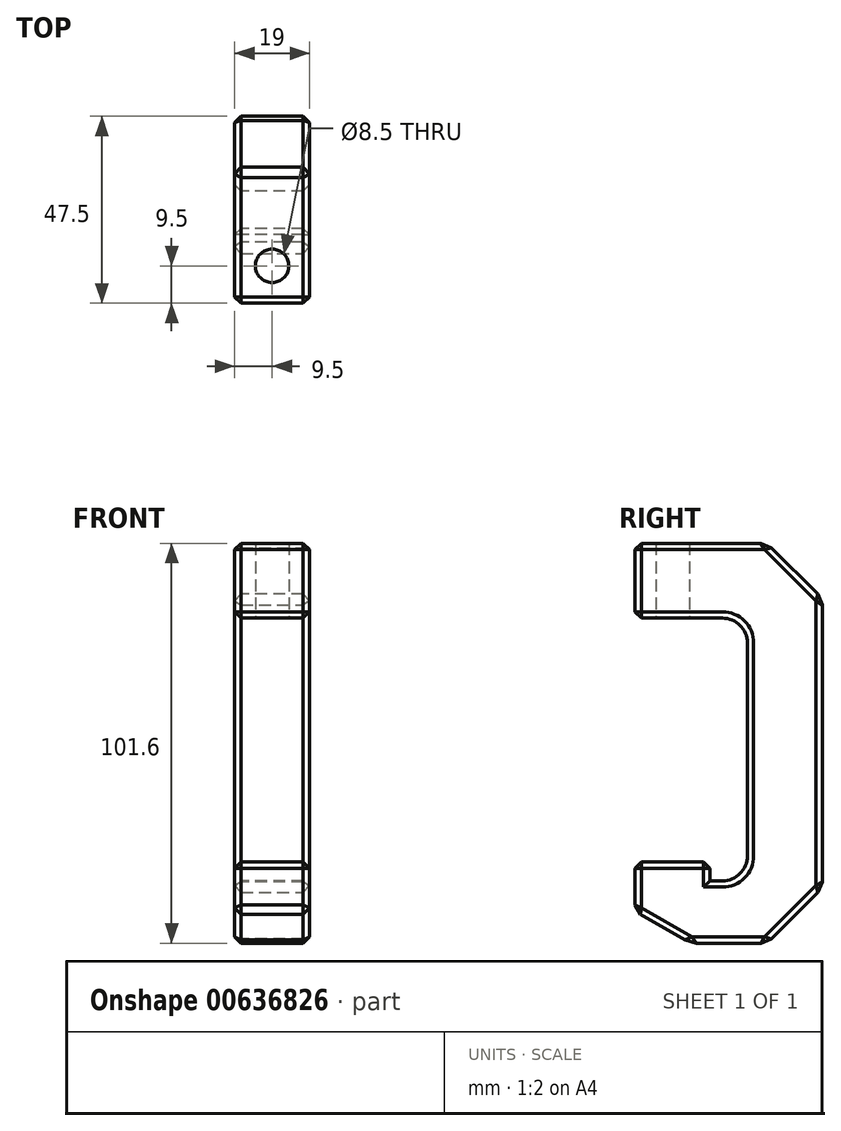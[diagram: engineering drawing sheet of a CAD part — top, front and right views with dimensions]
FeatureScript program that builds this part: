
annotation { "Feature Type Name" : "Feature", "Feature Type Description" : "" }
export const myFeature = defineFeature(function(context is Context, id is Id, definition is map)
    precondition{}
    {
        {
            var Q0;
            Q0=qCreatedBy(makeId("Right.planeOp"),FACE);
            var sketch = newSketch(context, id + "F0", { "sketchPlane" : qUnion([Q0])});
            skLineSegment(sketch, "E0", {"start": v(-33.5, 101.6) * mm, "end": v(-33.5, 82.6) * mm});
            skLineSegment(sketch, "E1", {"start": v(-33.5, 82.6) * mm, "end": v(-11.35, 82.6) * mm});
            skLineSegment(sketch, "E2", {"start": v(-5, 76.25) * mm, "end": v(-5, 22.2) * mm});
            skLineSegment(sketch, "E3", {"start": v(-11.35, 15.85) * mm, "end": v(-14.5, 15.85) * mm});
            skLineSegment(sketch, "E4", {"start": v(-33.5, 8.08) * mm, "end": v(-19.5, 0) * mm});
            skLineSegment(sketch, "E5", {"start": v(-19.5, 0) * mm, "end": v(0, 0) * mm});
            skLineSegment(sketch, "E6", {"start": v(0, 0) * mm, "end": v(14, 14) * mm});
            skLineSegment(sketch, "E7", {"start": v(14, 14) * mm, "end": v(14, 87.6) * mm});
            skLineSegment(sketch, "E8", {"start": v(14, 87.6) * mm, "end": v(0, 101.6) * mm});
            skLineSegment(sketch, "E9", {"start": v(0, 101.6) * mm, "end": v(-33.5, 101.6) * mm});
            skPoint(sketch, "E10.visualSharp", {"position": v(-5, 15.85) * mm});
            skArc(sketch, "E10.filletArc", {"start": v(-11.35, 15.85) * mm, "mid": v(-6.86, 17.7) * mm, "end": v(-5, 22.2) * mm});
            skPoint(sketch, "E11.visualSharp", {"position": v(-5, 82.6) * mm});
            skArc(sketch, "E11.filletArc", {"start": v(-5, 76.25) * mm, "mid": v(-6.86, 80.74) * mm, "end": v(-11.35, 82.6) * mm});
            skLineSegment(sketch, "E12", {"start": v(-14.5, 15.85) * mm, "end": v(-14.5, 20.65) * mm});
            skLineSegment(sketch, "E13", {"start": v(-14.5, 20.65) * mm, "end": v(-33.5, 20.65) * mm});
            skLineSegment(sketch, "E14", {"start": v(-33.5, 20.65) * mm, "end": v(-33.5, 8.08) * mm});
            skSolve(sketch);
        }
        {
            var Q0;
            Q0=makeQuery(id+"F0.imprint","IMPRINT",FACE,{"disambiguationData":[TD([[makeQuery(id+"F0.imprint","IMPRINT",EDGE,{"derivedFrom":sQuery(id+"F0.wireOp",EDGE,"E0")}),1.0]])]});
            extrude(context, id + "F1", {"entities" : qUnion([Q0]), "depth" : 19 * mm, "offsetDistance" : 25 * mm, "symmetric" : true});
        }
        {
            var Q0;
            Q0=makeQuery(id+"F1.opExtrude","SWEPT_FACE",FACE,{"disambiguationData":[OSD([sQuery(id+"F0.wireOp",EDGE,"E9")])]});
            var Q1;
            Q1=makeQuery(id+"F1.opExtrude","SWEPT_FACE",FACE,{"disambiguationData":[OSD([sQuery(id+"F0.wireOp",EDGE,"E0")])]});
            var Q2;
            Q2=makeQuery(id+"F1.opExtrude","CAP_FACE",FACE,{"disambiguationData":[OSD([sQuery(id+"F0.wireOp",EDGE,"E0"),sQuery(id+"F0.wireOp",EDGE,"E1"),sQuery(id+"F0.wireOp",EDGE,"E2"),sQuery(id+"F0.wireOp",EDGE,"E3"),sQuery(id+"F0.wireOp",EDGE,"E4"),sQuery(id+"F0.wireOp",EDGE,"E5"),sQuery(id+"F0.wireOp",EDGE,"E6"),sQuery(id+"F0.wireOp",EDGE,"E7"),sQuery(id+"F0.wireOp",EDGE,"E8"),sQuery(id+"F0.wireOp",EDGE,"E9"),sQuery(id+"F0.wireOp",EDGE,"E10.filletArc"),sQuery(id+"F0.wireOp",EDGE,"E11.filletArc"),sQuery(id+"F0.wireOp",EDGE,"E12"),sQuery(id+"F0.wireOp",EDGE,"E13"),sQuery(id+"F0.wireOp",EDGE,"E14")])],"isStart":false});
            var Q3;
            Q3=makeQuery(id+"F1.opExtrude","SWEPT_FACE",FACE,{"disambiguationData":[OSD([sQuery(id+"F0.wireOp",EDGE,"E13")])]});
            var Q4;
            Q4=makeQuery(id+"F1.opExtrude","SWEPT_FACE",FACE,{"disambiguationData":[OSD([sQuery(id+"F0.wireOp",EDGE,"E14")])]});
            var Q5;
            Q5=makeQuery(id+"F1.opExtrude","SWEPT_FACE",FACE,{"disambiguationData":[OSD([sQuery(id+"F0.wireOp",EDGE,"E8")])]});
            var Q6;
            Q6=makeQuery(id+"F1.opExtrude","SWEPT_FACE",FACE,{"disambiguationData":[OSD([sQuery(id+"F0.wireOp",EDGE,"E7")])]});
            var Q7;
            Q7=makeQuery(id+"F1.opExtrude","SWEPT_FACE",FACE,{"disambiguationData":[OSD([sQuery(id+"F0.wireOp",EDGE,"E6")])]});
            var Q8;
            Q8=makeQuery(id+"F1.opExtrude","SWEPT_FACE",FACE,{"disambiguationData":[OSD([sQuery(id+"F0.wireOp",EDGE,"E5")])]});
            var Q9;
            Q9=makeQuery(id+"F1.opExtrude","SWEPT_FACE",FACE,{"disambiguationData":[OSD([sQuery(id+"F0.wireOp",EDGE,"E4")])]});
            var Q10;
            Q10=makeQuery(id+"F1.opExtrude","CAP_FACE",FACE,{"disambiguationData":[OSD([sQuery(id+"F0.wireOp",EDGE,"E0"),sQuery(id+"F0.wireOp",EDGE,"E1"),sQuery(id+"F0.wireOp",EDGE,"E2"),sQuery(id+"F0.wireOp",EDGE,"E3"),sQuery(id+"F0.wireOp",EDGE,"E4"),sQuery(id+"F0.wireOp",EDGE,"E5"),sQuery(id+"F0.wireOp",EDGE,"E6"),sQuery(id+"F0.wireOp",EDGE,"E7"),sQuery(id+"F0.wireOp",EDGE,"E8"),sQuery(id+"F0.wireOp",EDGE,"E9"),sQuery(id+"F0.wireOp",EDGE,"E10.filletArc"),sQuery(id+"F0.wireOp",EDGE,"E11.filletArc"),sQuery(id+"F0.wireOp",EDGE,"E12"),sQuery(id+"F0.wireOp",EDGE,"E13"),sQuery(id+"F0.wireOp",EDGE,"E14")])],"isStart":true});
            chamfer(context, id + "F2", {"entities" : qUnion([Q0, Q1, Q2, Q3, Q4, Q5, Q6, Q7, Q8, Q9, Q10]), "width" : 1.6 * mm, "tangentPropagation" : true});
        }
        {
            var Q0;
            Q0=makeQuery(id+"F1.opExtrude","SWEPT_FACE",FACE,{"disambiguationData":[OSD([sQuery(id+"F0.wireOp",EDGE,"E9")])]});
            var sketch = newSketch(context, id + "F3", { "sketchPlane" : qUnion([Q0])});
            skPoint(sketch, "E15", {"position": v(0, -24) * mm});
            skSolve(sketch);
        }
        {
            var Q0;
            Q0=sQuery(id+"F3.wireOp",VERTEX,"E15");
            var Q1;
            Q1=makeQuery(id+"F1.opExtrude","SWEPT_BODY",BODY,{"disambiguationData":[OSD([sQuery(id+"F0.wireOp",EDGE,"E0"),sQuery(id+"F0.wireOp",EDGE,"E1"),sQuery(id+"F0.wireOp",EDGE,"E2"),sQuery(id+"F0.wireOp",EDGE,"E3"),sQuery(id+"F0.wireOp",EDGE,"E4"),sQuery(id+"F0.wireOp",EDGE,"E5"),sQuery(id+"F0.wireOp",EDGE,"E6"),sQuery(id+"F0.wireOp",EDGE,"E7"),sQuery(id+"F0.wireOp",EDGE,"E8"),sQuery(id+"F0.wireOp",EDGE,"E9"),sQuery(id+"F0.wireOp",EDGE,"E10.filletArc"),sQuery(id+"F0.wireOp",EDGE,"E11.filletArc"),sQuery(id+"F0.wireOp",EDGE,"E12"),sQuery(id+"F0.wireOp",EDGE,"E13"),sQuery(id+"F0.wireOp",EDGE,"E14")])]});
            hole(context, id + "F4", {"style" : HoleStyle.SIMPLE, "endStyle" : HoleEndStyle.BLIND, "standardTappedOrClearance" : lookupTablePath({ "standard" : "ISO", "engagement" : "75%", "pitch" : "1.5 mm", "size" : "M10", "type" : "Tapped" }), "standardBlindInLast" : lookupTablePath({ "standard" : "ISO", "engagement" : "75%", "pitch" : "1.5 mm", "size" : "M10", "type" : "Tapped" }), "holeDiameter" : 8.5 * mm, "majorDiameter" : 10 * mm, "showTappedDepth" : true, "holeDepth" : 30 * mm, "isTappedThrough" : true, "tappedDepth" : 25.5 * mm, "tapClearance" : 3, "locations" : qUnion([Q0]), "scope" : qUnion([Q1]), "startStyle" : HoleStartStyle.SKETCH});
        }
    });
